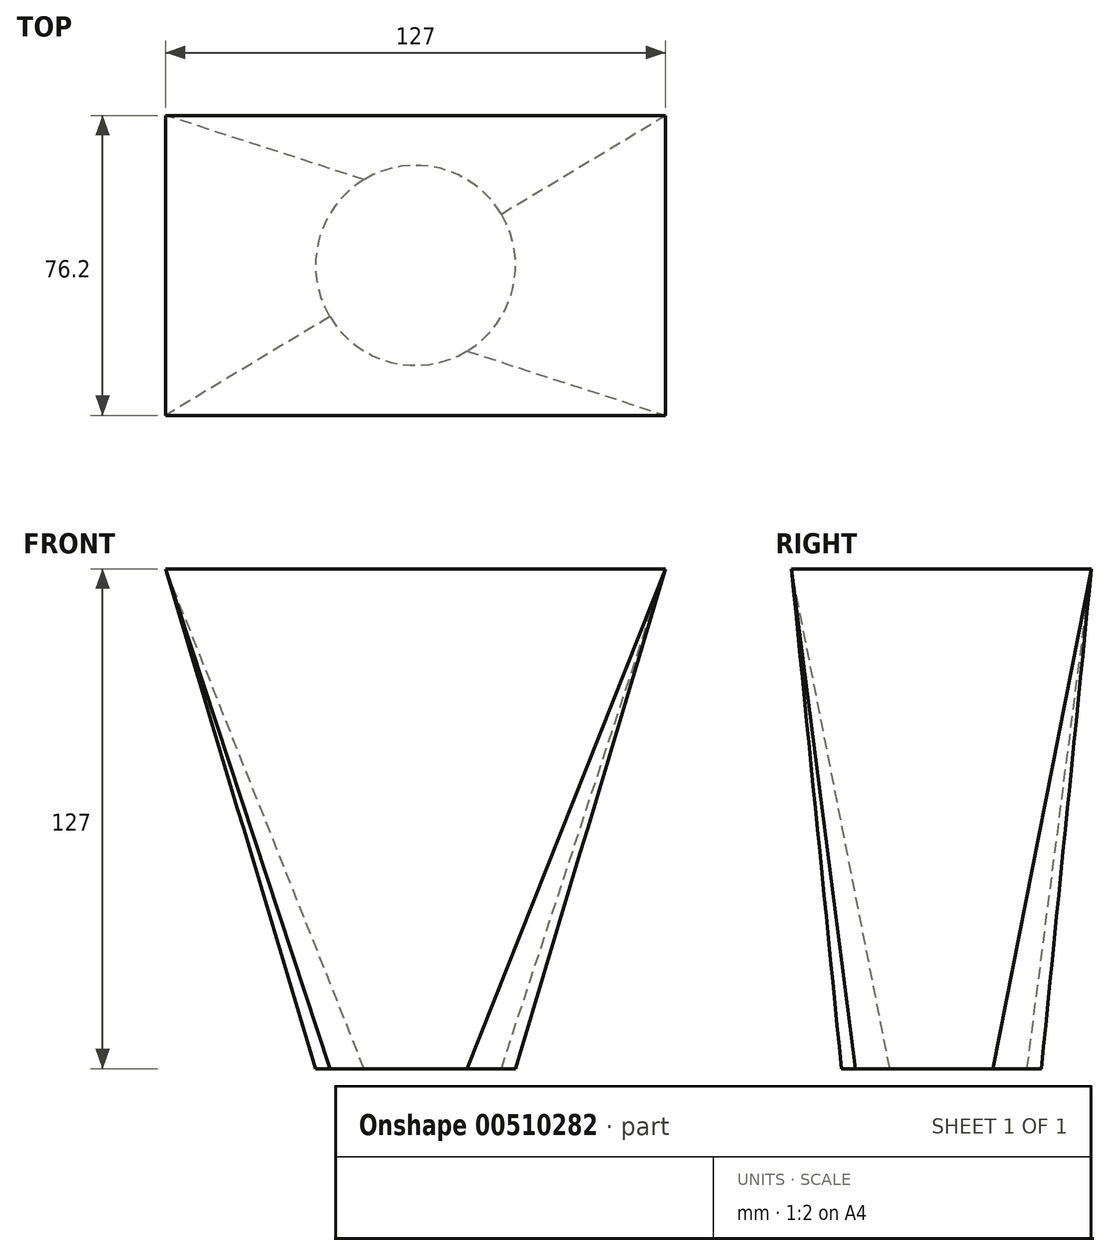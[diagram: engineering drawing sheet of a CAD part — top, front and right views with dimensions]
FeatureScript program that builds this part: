
annotation { "Feature Type Name" : "Feature", "Feature Type Description" : "" }
export const myFeature = defineFeature(function(context is Context, id is Id, definition is map)
    precondition{}
    {
        {
            var Q0;
            Q0=qCreatedBy(makeId("Top.planeOp"),FACE);
            var sketch = newSketch(context, id + "F0", { "sketchPlane" : qUnion([Q0])});
            skCircle(sketch, "E0", {"center": v(0, 0) * mm, "radius": 25.4 * mm});
            skSolve(sketch);
        }
        {
            var Q0;
            Q0=qCreatedBy(makeId("Top.planeOp"),FACE);
            cPlane(context, id + "F1", {"entities" : qUnion([Q0]), "cplaneType" : CPlaneType.OFFSET, "offset" : 127 * mm, "width" : 152.4 * mm, "height" : 152.4 * mm});
        }
        {
            var Q0;
            Q0=qCreatedBy(id+"F1.planeOp",FACE);
            var sketch = newSketch(context, id + "F2", { "sketchPlane" : qUnion([Q0])});
            skLineSegment(sketch, "E1.bottom", {"start": v(63.5, 38.1) * mm, "end": v(-63.5, 38.1) * mm});
            skLineSegment(sketch, "E1.top", {"start": v(63.5, -38.1) * mm, "end": v(-63.5, -38.1) * mm});
            skLineSegment(sketch, "E1.left", {"start": v(63.5, 38.1) * mm, "end": v(63.5, -38.1) * mm});
            skLineSegment(sketch, "E1.right", {"start": v(-63.5, 38.1) * mm, "end": v(-63.5, -38.1) * mm});
            skPoint(sketch, "E1.middle", {"position": v(0, 0) * mm});
            skSolve(sketch);
        }
        {
            var Q0;
            Q0=makeQuery(id+"F0.imprint","IMPRINT",FACE,{"disambiguationData":[TD([[makeQuery(id+"F0.imprint","IMPRINT",EDGE,{"derivedFrom":sQuery(id+"F0.wireOp",EDGE,"E0")}),1.0]])]});
            var Q1;
            Q1=makeQuery(id+"F2.imprint","IMPRINT",FACE,{"disambiguationData":[TD([[makeQuery(id+"F2.imprint","IMPRINT",EDGE,{"derivedFrom":sQuery(id+"F2.wireOp",EDGE,"E1.bottom")}),1.0]])]});
            loft(context, id + "F3", {"sheetProfilesArray" : [{ "sheetProfileEntities" : qUnion([Q0]) }, { "sheetProfileEntities" : qUnion([Q1]) }]});
        }
    });
